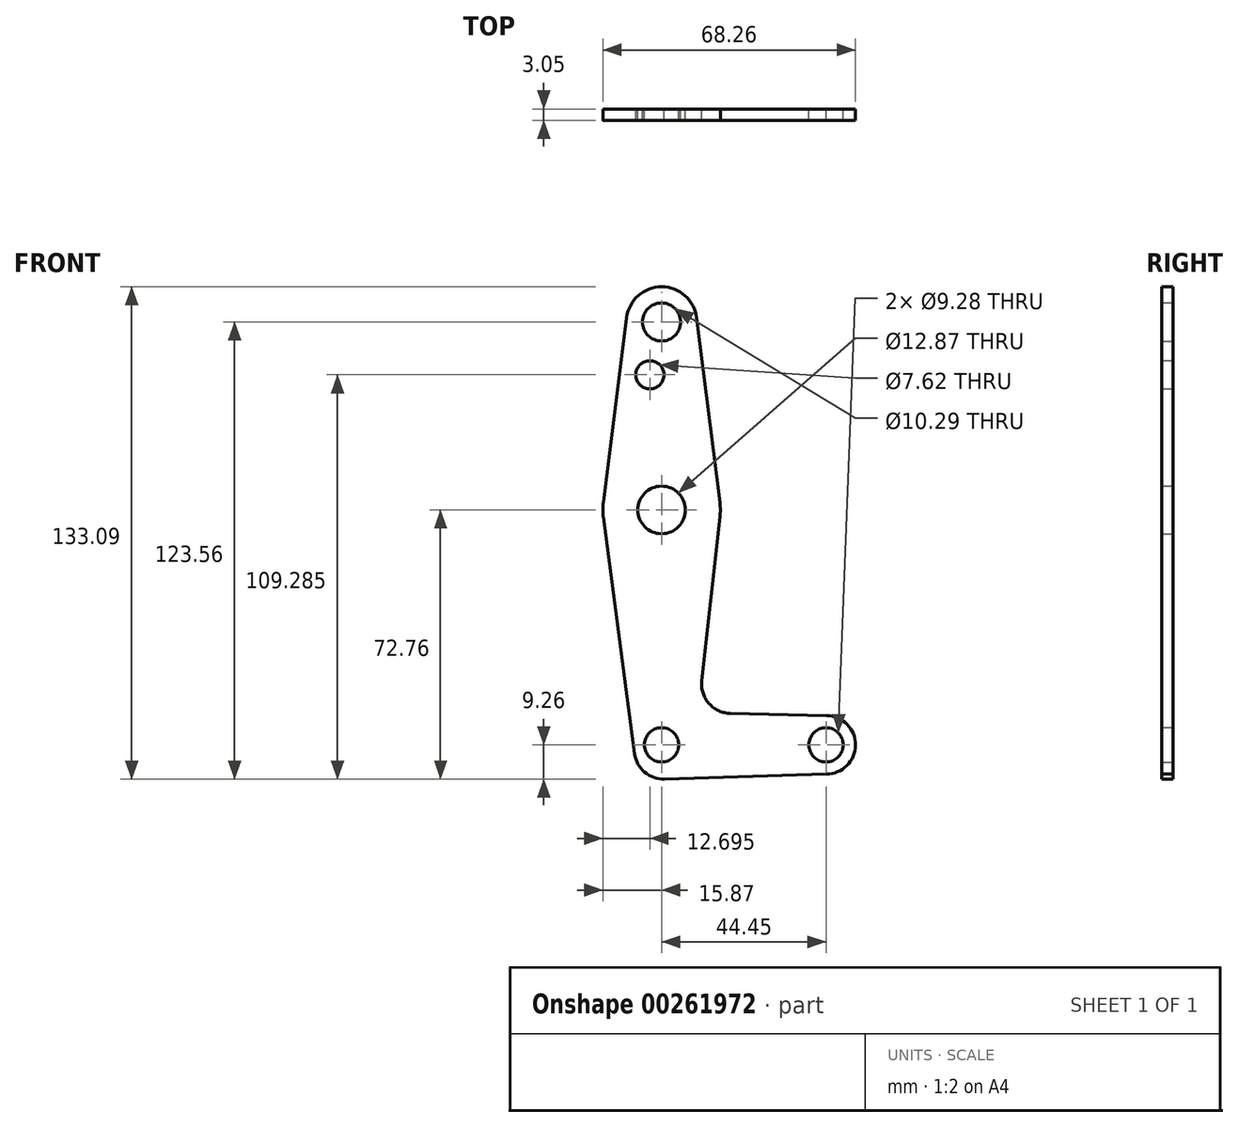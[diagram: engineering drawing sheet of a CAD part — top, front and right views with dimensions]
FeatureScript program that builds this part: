
annotation { "Feature Type Name" : "Feature", "Feature Type Description" : "" }
export const myFeature = defineFeature(function(context is Context, id is Id, definition is map)
    precondition{}
    {
        {
            var Q0;
            Q0=qCreatedBy(makeId("Front.planeOp"),FACE);
            var sketch = newSketch(context, id + "F0", { "sketchPlane" : qUnion([Q0])});
            skLineSegment(sketch, "E0", {"start": v(0, 114.3) * mm, "end": v(0, 63.5) * mm});
            skLineSegment(sketch, "E1", {"start": v(0, 63.5) * mm, "end": v(0, 0) * mm});
            skLineSegment(sketch, "E2", {"start": v(0, 0) * mm, "end": v(44.45, 0) * mm});
            skCircle(sketch, "E3", {"center": v(0, 114.3) * mm, "radius": 9.53 * mm});
            skCircle(sketch, "E4", {"center": v(0, 63.5) * mm, "radius": 15.88 * mm});
            skCircle(sketch, "E5", {"center": v(44.45, 0) * mm, "radius": 7.94 * mm});
            skLineSegment(sketch, "E6", {"start": v(9.45, 115.5) * mm, "end": v(15.75, 65.48) * mm});
            skLineSegment(sketch, "E7", {"start": v(-9.45, 115.5) * mm, "end": v(-15.75, 65.48) * mm});
            skLineSegment(sketch, "E8", {"start": v(0.79, -9.26) * mm, "end": v(44.5, -7.94) * mm});
            skCircle(sketch, "E9", {"center": v(-3.17, 100.03) * mm, "radius": 3.81 * mm});
            skLineSegment(sketch, "E10", {"start": v(18.6, 8.5) * mm, "end": v(44.62, 7.94) * mm});
            skLineSegment(sketch, "E11", {"start": v(-15.74, 61.43) * mm, "end": v(-7.33, -2.35) * mm});
            skLineSegment(sketch, "E12", {"start": v(15.78, 61.75) * mm, "end": v(10.86, 17.32) * mm});
            skCircle(sketch, "E13", {"center": v(0, 0) * mm, "radius": 4.64 * mm});
            skCircle(sketch, "E14", {"center": v(44.45, 0) * mm, "radius": 4.64 * mm});
            skArc(sketch, "E15.filletArc", {"start": v(10.86, 17.32) * mm, "mid": v(12.78, 11.2) * mm, "end": v(18.6, 8.5) * mm});
            skCircle(sketch, "E16", {"center": v(0, 63.5) * mm, "radius": 6.43 * mm});
            skCircle(sketch, "E17", {"center": v(0, 114.3) * mm, "radius": 5.15 * mm});
            skArc(sketch, "E18.filletArc", {"start": v(-7.33, -2.35) * mm, "mid": v(-4.6, -7.37) * mm, "end": v(0.79, -9.26) * mm});
            skSolve(sketch);
        }
        {
            var Q0;
            Q0 = qSketchRegion(id + "F0", true);
            extrude(context, id + "F1", {"entities" : qUnion([Q0]), "depth" : 3.05 * mm});
        }
    });
